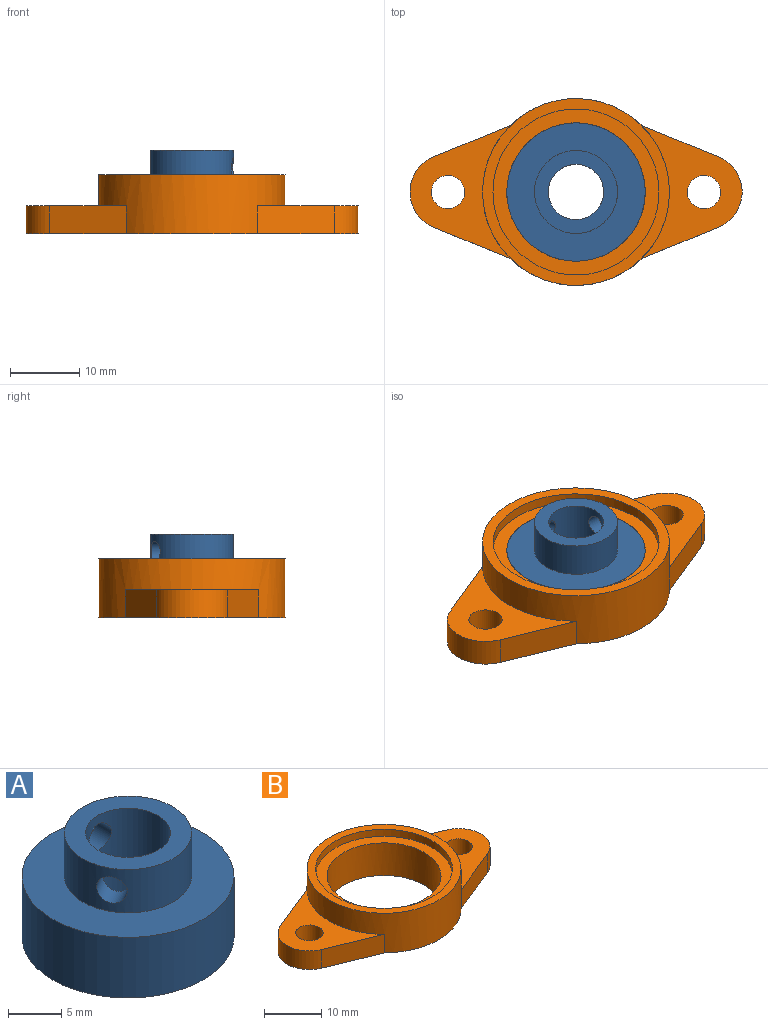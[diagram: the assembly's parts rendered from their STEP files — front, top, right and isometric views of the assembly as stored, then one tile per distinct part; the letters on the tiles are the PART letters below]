
ASSEMBLY  parts=2 mates=1
PART A: 8 faces, bbox 20x20x12 mm
  f0: cylinder r=6mm len=12mm, axis (0,0,-1), area 174.3mm2, adj f3,f4,f6,f7
  f1: plane 20x20mm, normal (0,0,-1), area 263.9mm2, adj f2,f5
  f2: cylinder r=4mm len=12mm, axis (0,0,-1), area 287.2mm2, adj f1,f3,f6,f7
  f3: plane 12x12mm, normal (0,0,1), area 62.8mm2, adj f0,f2
  f4: plane 20x20mm, normal (0,0,1), area 201.1mm2, adj f0,f5
  f5: cylinder r=10mm len=20mm, axis (0,0,-1), area 439.8mm2, adj f1,f4
  f6: cylinder r=1.5mm len=3mm, axis (0,-1,0), area 19.3mm2, adj f0,f2
  f7: cylinder r=1.5mm len=3.74mm, axis (0.87,0.5,0), area 19.3mm2, adj f0,f2
PART B: 16 faces, bbox 48x27x8.5 mm
  f0: plane 19.25x14.53mm, normal (0,0,1), area 117.1mm2, adj f1,f5,f6,f9,f10
  f1: plane 11.11x4.53mm, normal (0.38,0.93,0), area 48mm2, adj f0,f5,f9,f12
  f2: plane 11.11x4.53mm, normal (-0.38,0.93,0), area 48mm2, adj f3,f5,f11,f12
  f3: cylinder r=5.5mm len=10.19mm, axis (0,0,-1), area 52.1mm2, adj f2,f4,f11,f12
  f4: plane 11.11x4.53mm, normal (-0.38,-0.93,0), area 48mm2, adj f3,f5,f11,f12
  f5: cylinder r=13.5mm len=27mm, axis (0,0,-1), area 549.6mm2, adj f0,f1,f2,f4,f6,f11,f12,f15
  f6: plane 11.11x4.53mm, normal (0.38,-0.93,0), area 48mm2, adj f0,f5,f9,f12
  f7: cylinder r=2.4mm len=4.8mm, axis (0,0,-1), area 60.3mm2, adj f11,f12
  f8: cylinder r=10mm len=20mm, axis (0,0,-1), area 439.8mm2, adj f12,f13
  f9: cylinder r=5.5mm len=10.19mm, axis (0,0,-1), area 52.1mm2, adj f0,f1,f6,f12
  f10: cylinder r=2.4mm len=4.8mm, axis (0,0,-1), area 60.3mm2, adj f0,f12
  f11: plane 19.25x14.53mm, normal (0,0,1), area 117.1mm2, adj f2,f3,f4,f5,f7
  f12: plane 48x27mm, normal (0,0,-1), area 492.6mm2, adj f1,f2,f3,f4,f5,f6,f7,f8
  f13: plane 24x24mm, normal (0,0,1), area 138.2mm2, adj f8,f14
  f14: cylinder r=12mm len=24mm, axis (0,0,-1), area 113.1mm2, adj f13,f15
  f15: plane 27x27mm, normal (0,0,1), area 120.2mm2, adj f5,f14
PLACE A rot(axis=(0,0,-1),94.6deg) t=(0,0,0)mm
PLACE B at identity
MATE revolute A.f0 <-> B.f5  axis (0,0,1) through (0,0,7)mm
